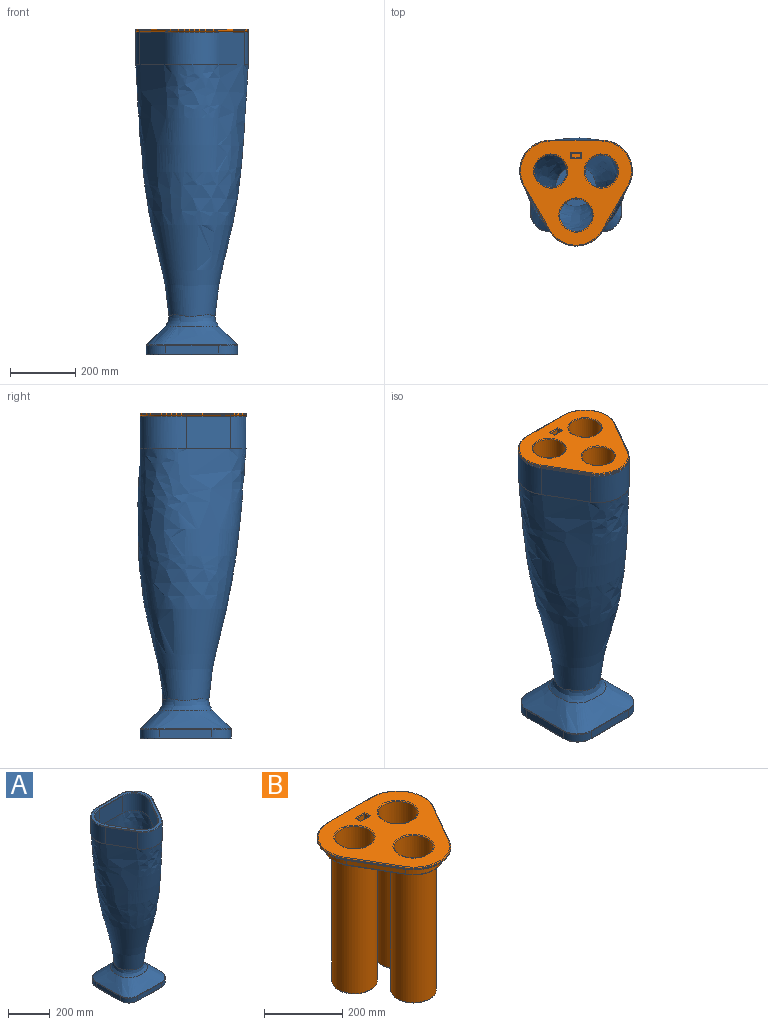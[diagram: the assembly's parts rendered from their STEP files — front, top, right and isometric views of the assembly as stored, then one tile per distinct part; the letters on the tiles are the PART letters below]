
ASSEMBLY  parts=2 mates=1
PART A: 60 faces, bbox 377.5x371.1x1008 mm
  f0: cylinder r=95mm len=142.5mm, axis (0,0,1), area 19598.3mm2, adj f1,f11,f28,f48
  f1: plane 155.99x98.6mm, normal (0,1,0), area 15354.6mm2, adj f0,f2,f27,f28,f30,f49
  f2: cylinder r=95mm len=142.5mm, axis (0,0,1), area 19598.3mm2, adj f1,f3,f30,f51
  f3: plane 135.1x98.6mm, normal (-0.87,-0.5,0), area 15354.6mm2, adj f2,f4,f27,f29,f30,f53
  f4: cylinder r=95mm len=164.55mm, axis (0,0,1), area 19598.3mm2, adj f3,f11,f29,f52
  f5: plane 135x98.5mm, normal (0.87,0.5,0), area 15354.6mm2, adj f6,f10,f16,f57
  f6: cylinder r=76mm len=114mm, axis (0,0,1), area 15678.6mm2, adj f5,f7,f16,f59
  f7: plane 155.88x98.5mm, normal (0,-1,0), area 15354.6mm2, adj f6,f8,f16,f58
  f8: cylinder r=76mm len=114mm, axis (0,0,1), area 15678.6mm2, adj f7,f9,f16,f56
  f9: plane 135x98.5mm, normal (-0.87,0.5,0), area 15354.6mm2, adj f8,f10,f16,f54
  f10: cylinder r=76mm len=131.64mm, axis (0,0,1), area 15678.6mm2, adj f5,f9,f16,f55
  f11: plane 135.1x98.6mm, normal (0.87,-0.5,0), area 15354.6mm2, adj f0,f4,f27,f28,f29,f50
  f12: plane 340.88x320mm, normal (0,0,1), area 14068.1mm2, adj f48,f49,f50,f51,f52,f53,f54,f55
  f13: plane 257.38x257.38mm, normal (0,0,1), area 63290.9mm2, adj f14
  f14: offset ~284.68x284.68mm, area 67272.8mm2, adj f13,f15
  f15: offset ~816.95x363.23mm, area 615229mm2, adj f14,f16
  f16: plane 329.78x308.96mm, normal (0,0,-1), area 10806.4mm2, adj f5,f6,f7,f8,f9,f10,f15
  f17: cylinder r=60mm len=60mm, axis (0,0,-1), area 2488.4mm2, adj f18,f24,f38,f46
  f18: plane 160x26.46mm, normal (0,-1,0), area 4230.8mm2, adj f17,f19,f36,f44
  f19: cylinder r=60mm len=60mm, axis (0,0,-1), area 2488.4mm2, adj f18,f20,f34,f42
  f20: plane 160x26.46mm, normal (1,0,0), area 4230.8mm2, adj f19,f21,f32,f40
  f21: cylinder r=60mm len=60mm, axis (0,0,-1), area 2488.4mm2, adj f20,f22,f33,f41
  f22: plane 160x26.46mm, normal (0,1,0), area 4230.8mm2, adj f21,f23,f35,f43
  f23: cylinder r=60mm len=60mm, axis (0,0,-1), area 2488.4mm2, adj f22,f24,f37,f45
  f24: plane 160x26.46mm, normal (-1,0,0), area 4230.8mm2, adj f17,f23,f39,f47
  f25: plane 275x275mm, normal (0,0,-1), area 72786.9mm2, adj f32,f33,f34,f35,f36,f37,f38,f39
  f26: bspline ~278.54x278.54mm, area 68166.7mm2, adj f31,f40,f41,f42,f43,f44,f45,f46
  f27: bspline ~773.43x345.21mm, area 644736.3mm2, adj f1,f3,f11,f28,f29,f30,f31
  f28: plane 149.2x97.61mm, normal (0,0,-1), area 8.7mm2, adj f0,f1,f11,f27
  f29: plane 169.73x54.19mm, normal (0,0,-1), area 9.5mm2, adj f3,f4,f11,f27
  f30: plane 144.76x102.73mm, normal (0,0,-1), area 9.8mm2, adj f1,f2,f3,f27
  f31: bspline ~163.83x163.78mm, area 17508.9mm2, adj f26,f27
  f32: cylinder r=2.5mm len=160mm, axis (0,1,0), area 628.3mm2, adj f20,f25,f33,f34
  f33: torus R=57.5mm, axis (0,0,1), area 364.5mm2, adj f21,f25,f32,f35
  f34: torus R=57.5mm, axis (0,0,1), area 364.5mm2, adj f19,f25,f32,f36
  f35: cylinder r=2.5mm len=160mm, axis (-1,0,0), area 628.3mm2, adj f22,f25,f33,f37
  f36: cylinder r=2.5mm len=160mm, axis (1,0,0), area 628.3mm2, adj f18,f25,f34,f38
  f37: torus R=57.5mm, axis (0,0,1), area 364.5mm2, adj f23,f25,f35,f39
  f38: torus R=57.5mm, axis (0,0,1), area 364.5mm2, adj f17,f25,f36,f39
  f39: cylinder r=2.5mm len=160mm, axis (0,-1,0), area 628.3mm2, adj f24,f25,f37,f38
  f40: bspline ~170.36x2.11mm, area 320.3mm2, adj f20,f26,f41,f42
  f41: bspline ~60.35x60.34mm, area 217.7mm2, adj f21,f26,f40,f43
  f42: bspline ~60.35x60.34mm, area 217.7mm2, adj f19,f26,f40,f44
  f43: bspline ~170.36x2.11mm, area 320.3mm2, adj f22,f26,f41,f45
  f44: bspline ~170.99x2.16mm, area 320.3mm2, adj f18,f26,f42,f46
  f45: bspline ~60.35x60.34mm, area 217.7mm2, adj f23,f26,f43,f47
  f46: bspline ~60.35x60.34mm, area 217.7mm2, adj f17,f26,f44,f47
  f47: bspline ~170.36x2.11mm, area 320.3mm2, adj f24,f26,f45,f46
  f48: torus R=92.5mm, axis (0,0,1), area 773.9mm2, adj f0,f12,f49,f50
  f49: cylinder r=2.5mm len=155.88mm, axis (-1,0,0), area 612.2mm2, adj f1,f12,f48,f51
  f50: cylinder r=2.5mm len=136.25mm, axis (0.5,0.87,0), area 612.2mm2, adj f11,f12,f48,f52
  f51: torus R=92.5mm, axis (0,0,1), area 773.9mm2, adj f2,f12,f49,f53
  f52: torus R=92.5mm, axis (0,0,1), area 773.9mm2, adj f4,f12,f50,f53
  f53: cylinder r=2.5mm len=136.25mm, axis (0.5,-0.87,0), area 612.2mm2, adj f3,f12,f51,f52
  f54: cylinder r=2.5mm len=136.25mm, axis (-0.5,-0.87,0), area 612.2mm2, adj f9,f12,f55,f56
  f55: torus R=78.5mm, axis (0,0,1), area 632.5mm2, adj f10,f12,f54,f57
  f56: torus R=78.5mm, axis (0,0,1), area 632.5mm2, adj f8,f12,f54,f58
  f57: cylinder r=2.5mm len=136.25mm, axis (-0.5,0.87,0), area 612.2mm2, adj f5,f12,f55,f59
  f58: cylinder r=2.5mm len=155.88mm, axis (1,0,0), area 612.2mm2, adj f7,f12,f56,f59
  f59: torus R=78.5mm, axis (0,0,1), area 632.5mm2, adj f6,f12,f57,f58
PART B: 101 faces, bbox 361.5x340.7x450 mm
  f0: plane 340.88x320mm, normal (0,0,1), area 53983.4mm2, adj f41,f42,f43,f44,f86,f87,f88,f89
  f1: plane 284.88x264mm, normal (0,0,-1), area 17473.9mm2, adj f49,f50,f51,f52,f53,f54,f55,f56
  f2: plane 340.88x320mm, normal (0,0,-1), area 15025.9mm2, adj f68,f69,f70,f71,f72,f73,f95,f96
  f3: cylinder r=95mm len=142.5mm, axis (0,0,1), area 596.9mm2, adj f4,f11,f93,f99
  f4: plane 135x77.94mm, normal (-0.87,-0.5,0), area 467.7mm2, adj f3,f5,f91,f97
  f5: cylinder r=95mm len=164.55mm, axis (0,0,1), area 596.9mm2, adj f4,f6,f89,f95
  f6: plane 135x77.94mm, normal (0.87,-0.5,0), area 467.7mm2, adj f5,f7,f90,f96
  f7: cylinder r=95mm len=142.5mm, axis (0,0,1), area 596.9mm2, adj f6,f11,f92,f98
  f8: cylinder r=50mm len=445mm, axis (0,0,1), area 139800.9mm2, adj f67,f87
  f9: cylinder r=50mm len=445mm, axis (0,0,1), area 139800.9mm2, adj f63,f86
  f10: cylinder r=50mm len=445mm, axis (0,0,1), area 139800.9mm2, adj f64,f88
  f11: plane 155.88x3mm, normal (0,1,0), area 467.7mm2, adj f3,f7,f94,f100
  f12: plane 155.88x25mm, normal (0,1,0), area 3897.1mm2, adj f13,f23,f73,f76
  f13: cylinder r=75mm len=112.5mm, axis (0,0,1), area 3927mm2, adj f12,f14,f72,f74
  f14: plane 135x77.94mm, normal (-0.87,-0.5,0), area 3897.1mm2, adj f13,f15,f70,f75
  f15: cylinder r=75mm len=129.9mm, axis (0,0,1), area 3927mm2, adj f14,f16,f68,f77
  f16: plane 135x77.94mm, normal (0.87,-0.5,0), area 3897.1mm2, adj f15,f23,f69,f79
  f17: cylinder r=67mm len=100.5mm, axis (0,0,1), area 3508.1mm2, adj f18,f22,f53,f83
  f18: plane 155.88x25mm, normal (0,-1,0), area 3897.1mm2, adj f17,f19,f56,f81
  f19: cylinder r=67mm len=100.5mm, axis (0,0,1), area 3508.1mm2, adj f18,f20,f52,f80
  f20: plane 135x77.94mm, normal (-0.87,0.5,0), area 3897.1mm2, adj f19,f21,f50,f82
  f21: cylinder r=67mm len=116.05mm, axis (0,0,1), area 3508.1mm2, adj f20,f22,f49,f84
  f22: plane 135x77.94mm, normal (0.87,0.5,0), area 3897.1mm2, adj f17,f21,f51,f85
  f23: cylinder r=75mm len=112.5mm, axis (0,0,1), area 3927mm2, adj f12,f16,f71,f78
  f24: plane 300.88x280mm, normal (0,0,-1), area 2741.3mm2, adj f74,f75,f76,f77,f78,f79,f80,f81
  f25: cylinder r=58mm len=437mm, axis (0,0,1), area 159253.6mm2, adj f61,f66
  f26: plane 111x111mm, normal (0,0,-1), area 1017.9mm2, adj f66,f67
  f27: cylinder r=58mm len=437mm, axis (0,0,1), area 159253.6mm2, adj f59,f62
  f28: plane 111x111mm, normal (0,0,-1), area 1017.9mm2, adj f62,f63
  f29: cylinder r=58mm len=437mm, axis (0,0,1), area 159253.6mm2, adj f55,f65
  f30: plane 111x111mm, normal (0,0,-1), area 1017.9mm2, adj f64,f65
  f31: plane 46x31mm, normal (0,0,-1), area 1426mm2, adj f32,f33,f34,f35
  f32: plane 46x29.5mm, normal (0,-1,0), area 1357mm2, adj f31,f33,f35,f58
  f33: plane 31x29.5mm, normal (-1,0,0), area 914.5mm2, adj f31,f32,f34,f54
  f34: plane 46x29.5mm, normal (0,1,0), area 1357mm2, adj f31,f33,f35,f57
  f35: plane 31x29.5mm, normal (1,0,0), area 914.5mm2, adj f31,f32,f34,f60
  f36: plane 33x30mm, normal (0,-1,0), area 990mm2, adj f37,f39,f41,f45
  f37: plane 33x15mm, normal (1,0,0), area 495mm2, adj f36,f38,f42,f46
  f38: plane 33x30mm, normal (0,1,0), area 990mm2, adj f37,f39,f44,f48
  f39: plane 33x15mm, normal (-1,0,0), area 495mm2, adj f36,f38,f43,f47
  f40: plane 25x10mm, normal (0,0,1), area 250mm2, adj f45,f46,f47,f48
  f41: cylinder r=2.5mm len=35mm, axis (1,0,0), area 124.9mm2, adj f0,f36,f42,f43
  f42: cylinder r=2.5mm len=20mm, axis (0,1,0), area 66mm2, adj f0,f37,f41,f44
  f43: cylinder r=2.5mm len=20mm, axis (0,-1,0), area 66mm2, adj f0,f39,f41,f44
  f44: cylinder r=2.5mm len=35mm, axis (-1,0,0), area 124.9mm2, adj f0,f38,f42,f43
  f45: cylinder r=2.5mm len=30mm, axis (-1,0,0), area 110.7mm2, adj f36,f40,f46,f47
  f46: cylinder r=2.5mm len=15mm, axis (0,-1,0), area 51.8mm2, adj f37,f40,f45,f48
  f47: cylinder r=2.5mm len=15mm, axis (0,1,0), area 51.8mm2, adj f39,f40,f45,f48
  f48: cylinder r=2.5mm len=30mm, axis (1,0,0), area 110.7mm2, adj f38,f40,f46,f47
  f49: torus R=64.5mm, axis (0,0,1), area 543.6mm2, adj f1,f21,f50,f51
  f50: cylinder r=2.5mm len=136.25mm, axis (-0.5,-0.87,0), area 612.2mm2, adj f1,f20,f49,f52
  f51: cylinder r=2.5mm len=136.25mm, axis (-0.5,0.87,0), area 612.2mm2, adj f1,f22,f49,f53
  f52: torus R=64.5mm, axis (0,0,1), area 543.6mm2, adj f1,f19,f50,f56
  f53: torus R=64.5mm, axis (0,0,1), area 543.6mm2, adj f1,f17,f51,f56
  f54: cylinder r=2.5mm len=35.36mm, axis (0,-1,0), area 128.6mm2, adj f1,f33,f55,f56,f57,f58
  f55: torus R=60.5mm, axis (0,0,1), area 1453.5mm2, adj f1,f29,f54,f58
  f56: cylinder r=2.5mm len=155.88mm, axis (1,0,0), area 586.7mm2, adj f1,f18,f52,f53,f54,f57,f60
  f57: cylinder r=2.5mm len=50mm, axis (-1,0,0), area 162.4mm2, adj f34,f54,f56,f60
  f58: cylinder r=2.5mm len=50.72mm, axis (1,0,0), area 187.7mm2, adj f1,f32,f54,f55,f59,f60
  f59: torus R=60.5mm, axis (0,0,1), area 1453.5mm2, adj f1,f27,f58,f60
  f60: cylinder r=2.5mm len=35.36mm, axis (0,1,0), area 128.6mm2, adj f1,f35,f56,f57,f58,f59
  f61: torus R=60.5mm, axis (0,0,1), area 1453.5mm2, adj f1,f25
  f62: torus R=55.5mm, axis (0,0,1), area 1408.7mm2, adj f27,f28
  f63: torus R=52.5mm, axis (0,0,1), area 1256.1mm2, adj f9,f28
  f64: torus R=52.5mm, axis (0,0,1), area 1256.1mm2, adj f10,f30
  f65: torus R=55.5mm, axis (0,0,1), area 1408.7mm2, adj f29,f30
  f66: torus R=55.5mm, axis (0,0,1), area 1408.7mm2, adj f25,f26
  f67: torus R=52.5mm, axis (0,0,1), area 1256.1mm2, adj f8,f26
  f68: torus R=77.5mm, axis (0,0,1), area 624.3mm2, adj f2,f15,f69,f70
  f69: cylinder r=2.5mm len=136.25mm, axis (0.5,0.87,0), area 612.2mm2, adj f2,f16,f68,f71
  f70: cylinder r=2.5mm len=136.25mm, axis (0.5,-0.87,0), area 612.2mm2, adj f2,f14,f68,f72
  f71: torus R=77.5mm, axis (0,0,1), area 624.3mm2, adj f2,f23,f69,f73
  f72: torus R=77.5mm, axis (0,0,1), area 624.3mm2, adj f2,f13,f70,f73
  f73: cylinder r=2.5mm len=155.88mm, axis (-1,0,0), area 612.2mm2, adj f2,f12,f71,f72
  f74: torus R=72.5mm, axis (0,0,1), area 609.4mm2, adj f13,f24,f75,f76
  f75: cylinder r=2.5mm len=136.25mm, axis (-0.5,0.87,0), area 612.2mm2, adj f14,f24,f74,f77
  f76: cylinder r=2.5mm len=155.88mm, axis (1,0,0), area 612.2mm2, adj f12,f24,f74,f78
  f77: torus R=72.5mm, axis (0,0,1), area 609.4mm2, adj f15,f24,f75,f79
  f78: torus R=72.5mm, axis (0,0,1), area 609.4mm2, adj f23,f24,f76,f79
  f79: cylinder r=2.5mm len=136.25mm, axis (-0.5,-0.87,0), area 612.2mm2, adj f16,f24,f77,f78
  f80: torus R=69.5mm, axis (0,0,1), area 558.5mm2, adj f19,f24,f81,f82
  f81: cylinder r=2.5mm len=155.88mm, axis (-1,0,0), area 612.2mm2, adj f18,f24,f80,f83
  f82: cylinder r=2.5mm len=136.25mm, axis (0.5,0.87,0), area 612.2mm2, adj f20,f24,f80,f84
  f83: torus R=69.5mm, axis (0,0,1), area 558.5mm2, adj f17,f24,f81,f85
  f84: torus R=69.5mm, axis (0,0,1), area 558.5mm2, adj f21,f24,f82,f85
  f85: cylinder r=2.5mm len=136.25mm, axis (0.5,-0.87,0), area 612.2mm2, adj f22,f24,f83,f84
  f86: torus R=52.5mm, axis (0,0,1), area 1256.1mm2, adj f0,f9
  f87: torus R=52.5mm, axis (0,0,1), area 1256.1mm2, adj f0,f8
  f88: torus R=52.5mm, axis (0,0,1), area 1256.1mm2, adj f0,f10
  f89: torus R=92.5mm, axis (0,0,1), area 773.9mm2, adj f0,f5,f90,f91
  f90: cylinder r=2.5mm len=136.25mm, axis (0.5,0.87,0), area 612.2mm2, adj f0,f6,f89,f92
  f91: cylinder r=2.5mm len=136.25mm, axis (0.5,-0.87,0), area 612.2mm2, adj f0,f4,f89,f93
  f92: torus R=92.5mm, axis (0,0,1), area 773.9mm2, adj f0,f7,f90,f94
  f93: torus R=92.5mm, axis (0,0,1), area 773.9mm2, adj f0,f3,f91,f94
  f94: cylinder r=2.5mm len=155.88mm, axis (-1,0,0), area 612.2mm2, adj f0,f11,f92,f93
  f95: torus R=92.5mm, axis (0,0,1), area 773.9mm2, adj f2,f5,f96,f97
  f96: cylinder r=2.5mm len=136.25mm, axis (-0.5,-0.87,0), area 612.2mm2, adj f2,f6,f95,f98
  f97: cylinder r=2.5mm len=136.25mm, axis (-0.5,0.87,0), area 612.2mm2, adj f2,f4,f95,f99
  f98: torus R=92.5mm, axis (0,0,1), area 773.9mm2, adj f2,f7,f96,f100
  f99: torus R=92.5mm, axis (0,0,1), area 773.9mm2, adj f2,f3,f97,f100
  f100: cylinder r=2.5mm len=155.88mm, axis (1,0,0), area 612.2mm2, adj f2,f11,f98,f99
PLACE A at identity
PLACE B at identity
MATE slider A.f12 <-> B.f1  axis (0,0,1) through (0,0,992)mm
